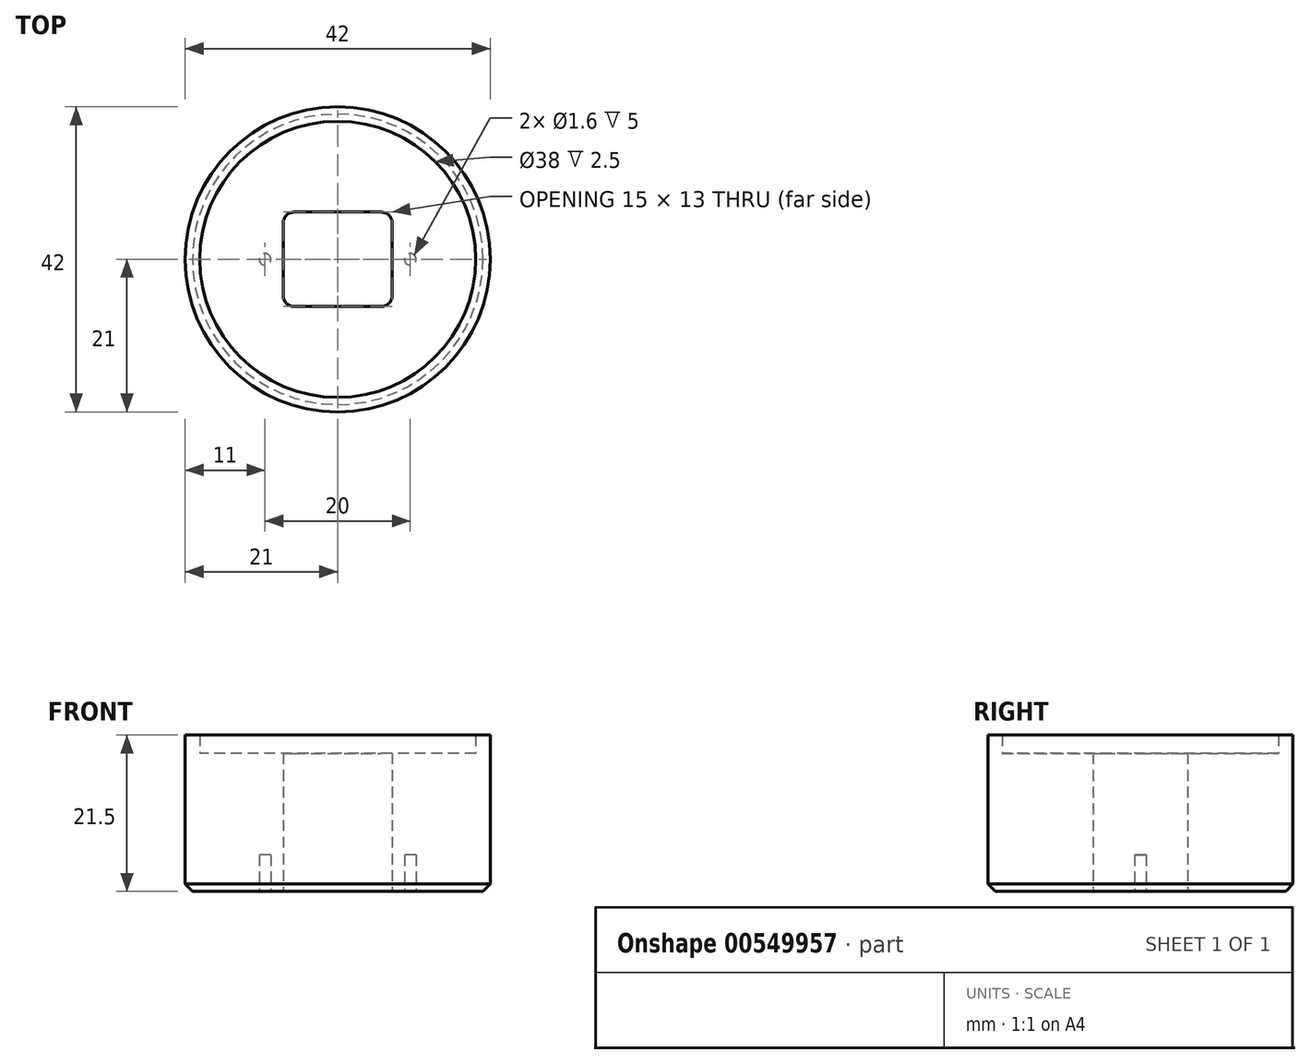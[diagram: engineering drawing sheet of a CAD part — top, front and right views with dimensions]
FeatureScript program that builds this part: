
annotation { "Feature Type Name" : "Feature", "Feature Type Description" : "" }
export const myFeature = defineFeature(function(context is Context, id is Id, definition is map)
    precondition{}
    {
        {
            var Q0;
            Q0=qCreatedBy(makeId("Top.planeOp"),FACE);
            var sketch = newSketch(context, id + "F0", { "sketchPlane" : qUnion([Q0])});
            skCircle(sketch, "E0", {"center": v(0, 0) * mm, "radius": 21 * mm});
            skCircle(sketch, "E1", {"center": v(-10, 0) * mm, "radius": 0.8 * mm});
            skCircle(sketch, "E2.1.0", {"center": v(10, 0) * mm, "radius": 0.8 * mm});
            skLineSegment(sketch, "E3.bottom", {"start": v(-6, -6.5) * mm, "end": v(6, -6.5) * mm});
            skLineSegment(sketch, "E3.top", {"start": v(-6, 6.5) * mm, "end": v(6, 6.5) * mm});
            skLineSegment(sketch, "E3.left", {"start": v(-7.5, -5) * mm, "end": v(-7.5, 5) * mm});
            skLineSegment(sketch, "E3.right", {"start": v(7.5, -5) * mm, "end": v(7.5, 5) * mm});
            skPoint(sketch, "E4.visualSharp", {"position": v(-7.5, 6.5) * mm});
            skArc(sketch, "E4.filletArc", {"start": v(-6, 6.5) * mm, "mid": v(-7.06, 6.06) * mm, "end": v(-7.5, 5) * mm});
            skPoint(sketch, "E5.visualSharp", {"position": v(7.5, 6.5) * mm});
            skArc(sketch, "E5.filletArc", {"start": v(7.5, 5) * mm, "mid": v(7.06, 6.06) * mm, "end": v(6, 6.5) * mm});
            skPoint(sketch, "E6.visualSharp", {"position": v(7.5, -6.5) * mm});
            skArc(sketch, "E6.filletArc", {"start": v(6, -6.5) * mm, "mid": v(7.06, -6.06) * mm, "end": v(7.5, -5) * mm});
            skPoint(sketch, "E7.visualSharp", {"position": v(-7.5, -6.5) * mm});
            skArc(sketch, "E7.filletArc", {"start": v(-7.5, -5) * mm, "mid": v(-7.06, -6.06) * mm, "end": v(-6, -6.5) * mm});
            skSolve(sketch);
        }
        {
            var Q0;
            Q0=makeQuery(id+"F0.imprint","IMPRINT",FACE,{"disambiguationData":[TD([[makeQuery(id+"F0.imprint","IMPRINT",EDGE,{"derivedFrom":sQuery(id+"F0.wireOp",EDGE,"E0")}),1.0]])]});
            extrude(context, id + "F1", {"entities" : qUnion([Q0]), "depth" : 5 * mm, "offsetDistance" : 25 * mm});
        }
        {
            var Q0;
            Q0=makeQuery(id+"F1.opExtrude","CAP_FACE",FACE,{"disambiguationData":[OSD([sQuery(id+"F0.wireOp",EDGE,"E0"),sQuery(id+"F0.wireOp",EDGE,"E1"),sQuery(id+"F0.wireOp",EDGE,"E2.1.0"),sQuery(id+"F0.wireOp",EDGE,"E3.bottom"),sQuery(id+"F0.wireOp",EDGE,"E3.top"),sQuery(id+"F0.wireOp",EDGE,"E3.left"),sQuery(id+"F0.wireOp",EDGE,"E3.right"),sQuery(id+"F0.wireOp",EDGE,"E4.filletArc"),sQuery(id+"F0.wireOp",EDGE,"E5.filletArc"),sQuery(id+"F0.wireOp",EDGE,"E6.filletArc"),sQuery(id+"F0.wireOp",EDGE,"E7.filletArc")])],"isStart":false});
            var sketch = newSketch(context, id + "F2", { "sketchPlane" : qUnion([Q0])});
            skCircle(sketch, "E8", {"center": v(0, 0) * mm, "radius": 21 * mm});
            skLineSegment(sketch, "E9.bottom", {"start": v(-6, -6.5) * mm, "end": v(6, -6.5) * mm});
            skLineSegment(sketch, "E9.top", {"start": v(-6, 6.5) * mm, "end": v(6, 6.5) * mm});
            skLineSegment(sketch, "E9.left", {"start": v(-7.5, -5) * mm, "end": v(-7.5, 5) * mm});
            skLineSegment(sketch, "E9.right", {"start": v(7.5, -5) * mm, "end": v(7.5, 5) * mm});
            skPoint(sketch, "E10.visualSharp", {"position": v(-7.5, 6.5) * mm});
            skArc(sketch, "E10.filletArc", {"start": v(-6, 6.5) * mm, "mid": v(-7.06, 6.06) * mm, "end": v(-7.5, 5) * mm});
            skPoint(sketch, "E11.visualSharp", {"position": v(7.5, 6.5) * mm});
            skArc(sketch, "E11.filletArc", {"start": v(7.5, 5) * mm, "mid": v(7.06, 6.06) * mm, "end": v(6, 6.5) * mm});
            skPoint(sketch, "E12.visualSharp", {"position": v(7.5, -6.5) * mm});
            skArc(sketch, "E12.filletArc", {"start": v(6, -6.5) * mm, "mid": v(7.06, -6.06) * mm, "end": v(7.5, -5) * mm});
            skPoint(sketch, "E13.visualSharp", {"position": v(-7.5, -6.5) * mm});
            skArc(sketch, "E13.filletArc", {"start": v(-7.5, -5) * mm, "mid": v(-7.06, -6.06) * mm, "end": v(-6, -6.5) * mm});
            skSolve(sketch);
        }
        {
            var Q0;
            Q0 = qSketchRegion(id + "F2", true);
            extrude(context, id + "F3", {"entities" : qUnion([Q0]), "operationType" : NewBodyOperationType.ADD, "depth" : 14 * mm, "offsetDistance" : 25 * mm});
        }
        {
            var Q0;
            Q0=makeQuery(id+"F3.opExtrude","CAP_FACE",FACE,{"disambiguationData":[OSD([sQuery(id+"F2.wireOp",EDGE,"E8"),sQuery(id+"F2.wireOp",EDGE,"E9.bottom"),sQuery(id+"F2.wireOp",EDGE,"E9.top"),sQuery(id+"F2.wireOp",EDGE,"E9.left"),sQuery(id+"F2.wireOp",EDGE,"E9.right"),sQuery(id+"F2.wireOp",EDGE,"E10.filletArc"),sQuery(id+"F2.wireOp",EDGE,"E11.filletArc"),sQuery(id+"F2.wireOp",EDGE,"E12.filletArc"),sQuery(id+"F2.wireOp",EDGE,"E13.filletArc")])],"isStart":false});
            var sketch = newSketch(context, id + "F4", { "sketchPlane" : qUnion([Q0])});
            skCircle(sketch, "E14", {"center": v(0, 0) * mm, "radius": 19 * mm});
            skCircle(sketch, "E15", {"center": v(0, 0) * mm, "radius": 21 * mm});
            skSolve(sketch);
        }
        {
            var Q0;
            Q0=makeQuery(id+"F4.imprint","IMPRINT",FACE,{"disambiguationData":[TD([[makeQuery(id+"F4.imprint","IMPRINT",EDGE,{"derivedFrom":sQuery(id+"F4.wireOp",EDGE,"E14")}),-1.0]])]});
            extrude(context, id + "F5", {"entities" : qUnion([Q0]), "operationType" : NewBodyOperationType.ADD, "depth" : 2.5 * mm, "offsetDistance" : 25 * mm});
        }
        {
            var Q0;
            Q0=makeQuery(id+"F1.opExtrude","CAP_EDGE",EDGE,{"disambiguationData":[OSD([sQuery(id+"F0.wireOp",EDGE,"E0")])],"isStart":true});
            chamfer(context, id + "F6", {"entities" : qUnion([Q0]), "width" : 1 * mm, "tangentPropagation" : true});
        }
    });
